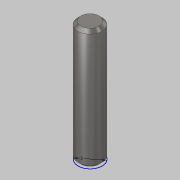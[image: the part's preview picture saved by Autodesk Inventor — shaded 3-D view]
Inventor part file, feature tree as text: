
AUTODESK INVENTOR PART (.ipt)
format: ipt  version: 2019.2 (Build 232265000, 265)  size: 99,840 bytes
history: native  units: mm
features: sketch x1, extrude x1, chamfer x1
ambient origin geometry x8: Origin, YZ Plane, XZ Plane, XY Plane, X Axis, Y Axis, Z Axis, Center Point
bodies: Volumenkörper1 (feature_tree)
feature tree (3):
  sketch  "Skizze1"  dims[d0=2.0mm d2=0.0mm d3=0.25mm d4=2.0mm d5=45.0deg]
  extrude  "Extrusion1"  TaperAngle=0.0deg  [1 undecoded]
  chamfer  "Fase1"  Distance=0.25mm Angle=45.0deg
note: 1 required parameter value undecoded (feature->parameter linkage not recoverable at this tier; creation-order binding heuristic only, values carry confidence <= 0.55)
